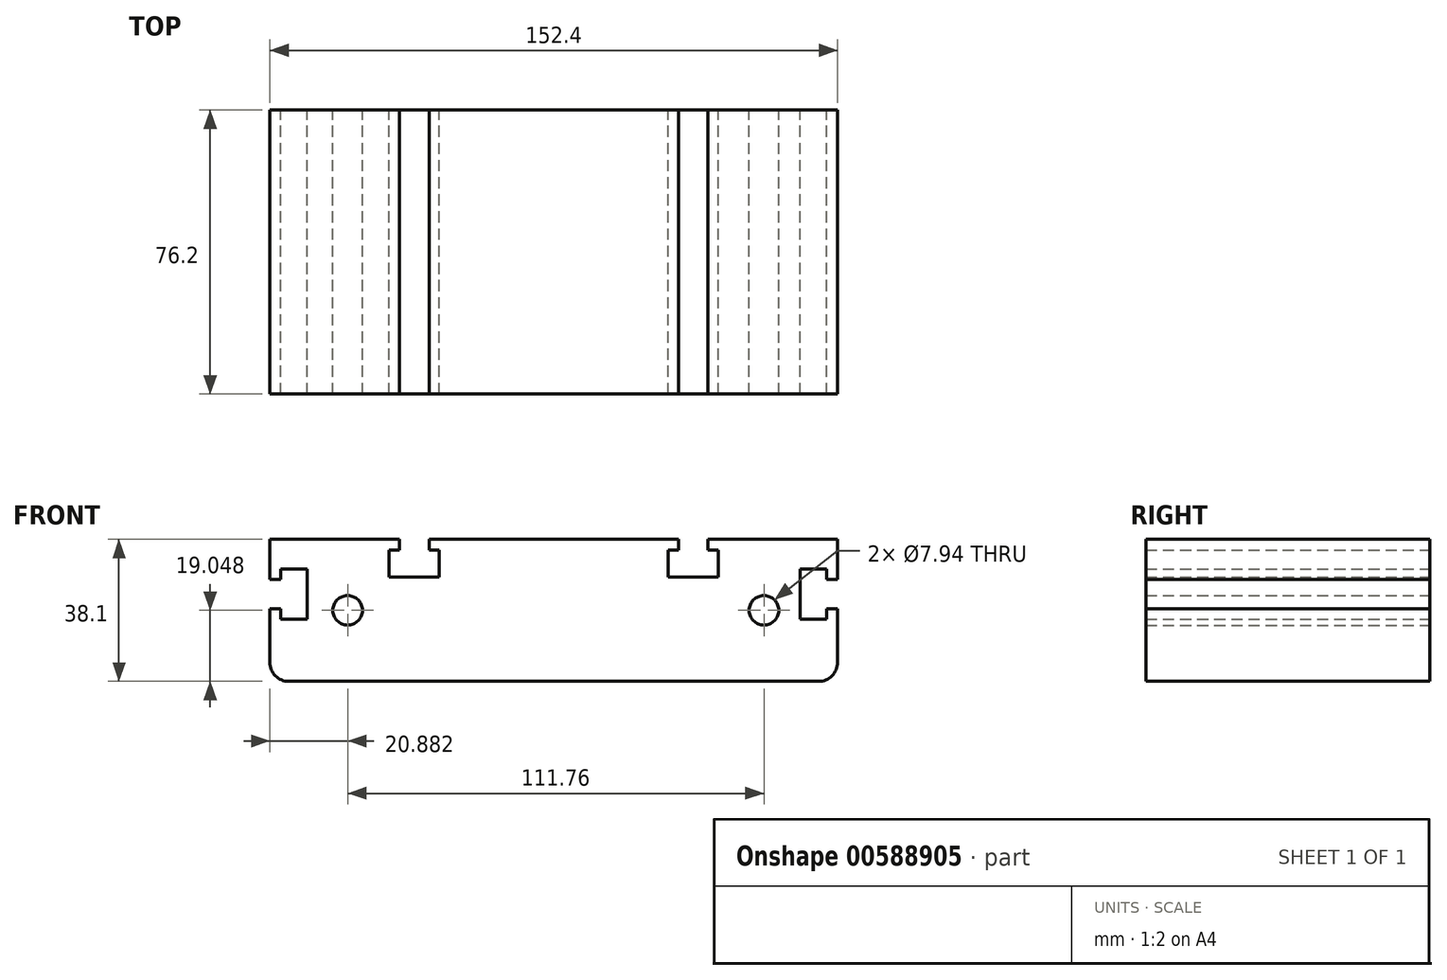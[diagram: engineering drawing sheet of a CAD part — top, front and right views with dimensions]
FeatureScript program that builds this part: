
annotation { "Feature Type Name" : "Feature", "Feature Type Description" : "" }
export const myFeature = defineFeature(function(context is Context, id is Id, definition is map)
    precondition{}
    {
        {
            var Q0;
            Q0=qCreatedBy(makeId("Front.planeOp"),FACE);
            var sketch = newSketch(context, id + "F0", { "sketchPlane" : qUnion([Q0])});
            skLineSegment(sketch, "E0.bottom", {"start": v(-76.64, 44.96) * mm, "end": v(-41.85, 44.96) * mm});
            skLineSegment(sketch, "E0.top", {"start": v(-69.02, -38.86) * mm, "end": v(68.14, -38.86) * mm});
            skLineSegment(sketch, "E0.left", {"start": v(-76.64, 44.96) * mm, "end": v(-76.64, 34.26) * mm});
            skLineSegment(sketch, "E0.right", {"start": v(75.76, 44.96) * mm, "end": v(75.76, 34.26) * mm});
            skLineSegment(sketch, "E1", {"start": v(-44.61, 42.06) * mm, "end": v(-41.85, 42.06) * mm});
            skLineSegment(sketch, "E2", {"start": v(-44.61, 34.9) * mm, "end": v(-31.15, 34.9) * mm});
            skLineSegment(sketch, "E3", {"start": v(-41.85, 44.96) * mm, "end": v(-41.85, 42.06) * mm});
            skLineSegment(sketch, "E4", {"start": v(-33.9, 44.96) * mm, "end": v(-33.9, 42.06) * mm});
            skLineSegment(sketch, "E5", {"start": v(-44.61, 42.06) * mm, "end": v(-44.61, 34.9) * mm});
            skLineSegment(sketch, "E6", {"start": v(-31.15, 42.06) * mm, "end": v(-31.15, 34.9) * mm});
            skLineSegment(sketch, "E7.trimOffspring", {"start": v(-33.9, 44.96) * mm, "end": v(33.02, 44.96) * mm});
            skLineSegment(sketch, "E8.trimOffspring", {"start": v(-33.9, 42.06) * mm, "end": v(-31.15, 42.06) * mm});
            skLineSegment(sketch, "E9.MirrorCS", {"start": v(33.02, 44.96) * mm, "end": v(33.02, 42.06) * mm});
            skLineSegment(sketch, "E10.MirrorCS", {"start": v(40.96, 44.96) * mm, "end": v(40.96, 42.06) * mm});
            skLineSegment(sketch, "E11.MirrorCS", {"start": v(43.73, 42.06) * mm, "end": v(43.73, 34.9) * mm});
            skLineSegment(sketch, "E12.MirrorCS", {"start": v(30.27, 42.06) * mm, "end": v(30.27, 34.9) * mm});
            skLineSegment(sketch, "E13.trimOffspring", {"start": v(40.96, 44.96) * mm, "end": v(75.76, 44.96) * mm});
            skLineSegment(sketch, "E14.trimOffspring", {"start": v(40.96, 42.06) * mm, "end": v(43.73, 42.06) * mm});
            skLineSegment(sketch, "E15.trimOffspring", {"start": v(30.27, 42.06) * mm, "end": v(33.02, 42.06) * mm});
            skLineSegment(sketch, "E16.trimOffspring", {"start": v(30.27, 34.9) * mm, "end": v(43.73, 34.9) * mm});
            skLineSegment(sketch, "E17", {"start": v(-73.75, 37.03) * mm, "end": v(-73.75, 34.26) * mm});
            skLineSegment(sketch, "E18", {"start": v(-73.75, 23.57) * mm, "end": v(-66.58, 23.57) * mm});
            skLineSegment(sketch, "E19", {"start": v(-66.58, 23.57) * mm, "end": v(-66.58, 37.03) * mm});
            skLineSegment(sketch, "E20", {"start": v(-66.58, 37.03) * mm, "end": v(-73.75, 37.03) * mm});
            skLineSegment(sketch, "E21", {"start": v(-73.75, 34.26) * mm, "end": v(-76.64, 34.26) * mm});
            skLineSegment(sketch, "E22", {"start": v(-73.75, 26.31) * mm, "end": v(-76.64, 26.31) * mm});
            skPoint(sketch, "E23.orphan", {"position": v(-73.75, 44.96) * mm});
            skLineSegment(sketch, "E24.trimOffspring", {"start": v(-73.75, 26.31) * mm, "end": v(-73.75, 23.57) * mm});
            skLineSegment(sketch, "E25.trimOffspring", {"start": v(-76.64, 26.31) * mm, "end": v(-76.64, -31.24) * mm});
            skLineSegment(sketch, "E26.MirrorCS", {"start": v(72.86, 26.31) * mm, "end": v(75.76, 26.31) * mm});
            skLineSegment(sketch, "E27.MirrorCS", {"start": v(72.86, 26.31) * mm, "end": v(72.86, 23.57) * mm});
            skLineSegment(sketch, "E28.MirrorCS", {"start": v(72.86, 37.03) * mm, "end": v(72.86, 34.26) * mm});
            skLineSegment(sketch, "E29.MirrorCS", {"start": v(72.86, 34.26) * mm, "end": v(75.76, 34.26) * mm});
            skLineSegment(sketch, "E30.MirrorCS", {"start": v(65.7, 37.03) * mm, "end": v(72.86, 37.03) * mm});
            skLineSegment(sketch, "E31.MirrorCS", {"start": v(65.7, 23.57) * mm, "end": v(65.7, 37.03) * mm});
            skLineSegment(sketch, "E32.MirrorCS", {"start": v(72.86, 23.57) * mm, "end": v(65.7, 23.57) * mm});
            skLineSegment(sketch, "E33.trimOffspring", {"start": v(75.76, 26.31) * mm, "end": v(75.76, -31.24) * mm});
            skCircle(sketch, "E34", {"center": v(-55.76, 25.9) * mm, "radius": 3.97 * mm});
            skCircle(sketch, "E35", {"center": v(56, 25.9) * mm, "radius": 3.97 * mm});
            skLineSegment(sketch, "E36", {"start": v(-76.64, -31.24) * mm, "end": v(-69.02, -38.86) * mm});
            skPoint(sketch, "E37.orphan", {"position": v(-76.64, -38.86) * mm});
            skLineSegment(sketch, "E38", {"start": v(68.14, -38.86) * mm, "end": v(75.76, -31.24) * mm});
            skPoint(sketch, "E39.orphan", {"position": v(75.76, -38.86) * mm});
            skLineSegment(sketch, "E40", {"start": v(-76.64, 6.86) * mm, "end": v(75.76, 6.86) * mm});
            skSolve(sketch);
        }
        {
            var Q0;
            Q0=makeQuery(id+"F0.imprint","IMPRINT",FACE,{"disambiguationData":[TD([[makeQuery(id+"F0.imprint","IMPRINT",EDGE,{"derivedFrom":sQuery(id+"F0.wireOp",EDGE,"E0.bottom")}),-1.0]])]});
            extrude(context, id + "F1", {"entities" : qUnion([Q0]), "depth" : 76.2 * mm, "offsetDistance" : 25.4 * mm});
        }
        {
            var Q0;
            Q0=makeQuery(id+"F1.opExtrude","SWEPT_EDGE",EDGE,{"disambiguationData":[OSD([sQuery(id+"F0.wireOp",EDGE,"E25.trimOffspring"),sQuery(id+"F0.wireOp",EDGE,"E40")])]});
            var Q1;
            Q1=makeQuery(id+"F1.opExtrude","SWEPT_EDGE",EDGE,{"disambiguationData":[OSD([sQuery(id+"F0.wireOp",EDGE,"E33.trimOffspring"),sQuery(id+"F0.wireOp",EDGE,"E40")])]});
            fillet(context, id + "F2", {"entities" : qUnion([Q0, Q1]), "radius" : 5.08 * mm, "tangentPropagation" : true, "allowEdgeOverflow" : false});
        }
    });
